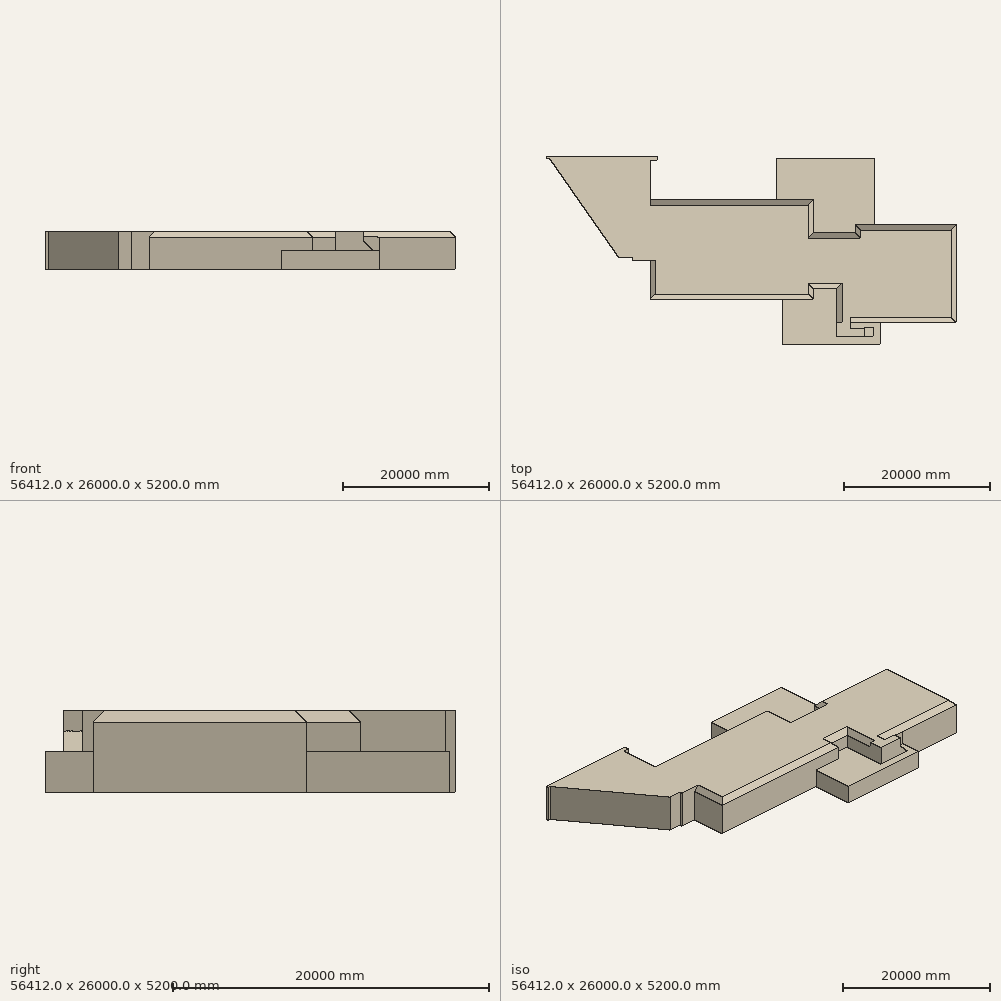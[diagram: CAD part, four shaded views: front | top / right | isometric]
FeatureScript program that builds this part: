
annotation { "Feature Type Name" : "Feature", "Feature Type Description" : "" }
export const myFeature = defineFeature(function(context is Context, id is Id, definition is map)
    precondition{}
    {
        {
            var Q0;
            Q0=qCreatedBy(makeId("Top.planeOp"),FACE);
            var sketch = newSketch(context, id + "F0", { "sketchPlane" : qUnion([Q0])});
            skLineSegment(sketch, "E0", {"start": v(36993.9, 16220.68) * mm, "end": v(36993.9, 2680.68) * mm});
            skLineSegment(sketch, "E1", {"start": v(36993.9, 2680.68) * mm, "end": v(26593.9, 2680.68) * mm});
            skLineSegment(sketch, "E2", {"start": v(26593.9, 2680.68) * mm, "end": v(26593.9, -349.32) * mm});
            skLineSegment(sketch, "E3", {"start": v(26593.9, -349.32) * mm, "end": v(13053.9, -349.32) * mm});
            skLineSegment(sketch, "E4", {"start": v(13053.9, -349.32) * mm, "end": v(13053.9, 5900.68) * mm});
            skLineSegment(sketch, "E5", {"start": v(13053.9, 5900.68) * mm, "end": v(-5146.1, 5900.68) * mm});
            skLineSegment(sketch, "E6", {"start": v(-5146.1, 5900.68) * mm, "end": v(-5146.1, 11220.68) * mm});
            skLineSegment(sketch, "E7", {"start": v(-5146.1, 11220.68) * mm, "end": v(-7546.1, 11220.68) * mm});
            skLineSegment(sketch, "E8", {"start": v(-7546.1, 11220.68) * mm, "end": v(-7546.1, 11620.68) * mm});
            skLineSegment(sketch, "E9", {"start": v(-7546.1, 11620.68) * mm, "end": v(-9442.1, 11620.68) * mm});
            skLineSegment(sketch, "E10", {"start": v(-9442.1, 11620.68) * mm, "end": v(-9442.1, 25270.68) * mm});
            skLineSegment(sketch, "E11", {"start": v(-9442.1, 25270.68) * mm, "end": v(-18978.1, 25270.68) * mm});
            skLineSegment(sketch, "E12", {"start": v(-18978.1, 25270.68) * mm, "end": v(-9442.1, 11620.68) * mm});
            skLineSegment(sketch, "E13", {"start": v(-18978.1, 25270.68) * mm, "end": v(-19418.1, 25270.68) * mm});
            skLineSegment(sketch, "E14", {"start": v(-19418.1, 25270.68) * mm, "end": v(-19418.1, 25650.68) * mm});
            skLineSegment(sketch, "E15", {"start": v(-19418.1, 25650.68) * mm, "end": v(-4148.1, 25650.68) * mm});
            skLineSegment(sketch, "E16", {"start": v(-4148.1, 25650.68) * mm, "end": v(-4148.1, 25040.68) * mm});
            skLineSegment(sketch, "E17", {"start": v(-4148.1, 25040.68) * mm, "end": v(-5048.1, 25040.68) * mm});
            skLineSegment(sketch, "E18", {"start": v(-5048.1, 25040.68) * mm, "end": v(-5048.1, 19620.68) * mm});
            skLineSegment(sketch, "E19", {"start": v(-5048.1, 19620.68) * mm, "end": v(12161.9, 19620.68) * mm});
            skLineSegment(sketch, "E20", {"start": v(12161.9, 19620.68) * mm, "end": v(12161.9, 25270.68) * mm});
            skLineSegment(sketch, "E21", {"start": v(12161.9, 25270.68) * mm, "end": v(25701.9, 25270.68) * mm});
            skLineSegment(sketch, "E22", {"start": v(25701.9, 25270.68) * mm, "end": v(25701.9, 15461.87) * mm});
            skLineSegment(sketch, "E23", {"start": v(36993.9, 16220.68) * mm, "end": v(25701.9, 16220.68) * mm});
            skSolve(sketch);
        }
        {
            var Q0;
            Q0=makeQuery(id+"F0.imprint","IMPRINT",FACE,{"disambiguationData":[TD([[makeQuery(id+"F0.imprint","IMPRINT",EDGE,{"derivedFrom":sQuery(id+"F0.wireOp",EDGE,"E0")}),-1.0]])]});
            var Q1;
            Q1=makeQuery(id+"F0.imprint","IMPRINT",FACE,{"disambiguationData":[TD([[makeQuery(id+"F0.imprint","IMPRINT",EDGE,{"derivedFrom":sQuery(id+"F0.wireOp",EDGE,"E10")}),1.0]])]});
            extrude(context, id + "F1", {"entities" : qUnion([Q0, Q1]), "depth" : 2600 * mm});
        }
        {
            var Q0;
            Q0=makeQuery(id+"F1.opExtrude","CAP_FACE",FACE,{"disambiguationData":[OSD([sQuery(id+"F0.wireOp",EDGE,"E0"),sQuery(id+"F0.wireOp",EDGE,"E1"),sQuery(id+"F0.wireOp",EDGE,"E2"),sQuery(id+"F0.wireOp",EDGE,"E3"),sQuery(id+"F0.wireOp",EDGE,"E4"),sQuery(id+"F0.wireOp",EDGE,"E5"),sQuery(id+"F0.wireOp",EDGE,"E6"),sQuery(id+"F0.wireOp",EDGE,"E7"),sQuery(id+"F0.wireOp",EDGE,"E8"),sQuery(id+"F0.wireOp",EDGE,"E9"),sQuery(id+"F0.wireOp",EDGE,"E12"),sQuery(id+"F0.wireOp",EDGE,"E13"),sQuery(id+"F0.wireOp",EDGE,"E14"),sQuery(id+"F0.wireOp",EDGE,"E15"),sQuery(id+"F0.wireOp",EDGE,"E16"),sQuery(id+"F0.wireOp",EDGE,"E17"),sQuery(id+"F0.wireOp",EDGE,"E18"),sQuery(id+"F0.wireOp",EDGE,"E19"),sQuery(id+"F0.wireOp",EDGE,"E20"),sQuery(id+"F0.wireOp",EDGE,"E21"),sQuery(id+"F0.wireOp",EDGE,"E22"),sQuery(id+"F0.wireOp",EDGE,"E23")])],"isStart":false});
            var sketch = newSketch(context, id + "F2", { "sketchPlane" : qUnion([Q0])});
            skLineSegment(sketch, "E24", {"start": v(12161.9, 19620.68) * mm, "end": v(17361.9, 19620.68) * mm});
            skLineSegment(sketch, "E25", {"start": v(17361.9, 19620.68) * mm, "end": v(17361.9, 15085.94) * mm});
            skLineSegment(sketch, "E26", {"start": v(17361.9, 15085.94) * mm, "end": v(23051.54, 15085.94) * mm});
            skLineSegment(sketch, "E27", {"start": v(23051.54, 15085.94) * mm, "end": v(23051.54, 16220.68) * mm});
            skLineSegment(sketch, "E28", {"start": v(23051.54, 16220.68) * mm, "end": v(25701.9, 16220.68) * mm});
            skLineSegment(sketch, "E29", {"start": v(13053.9, 5900.68) * mm, "end": v(17361.9, 5900.68) * mm});
            skLineSegment(sketch, "E30", {"start": v(17361.9, 5900.68) * mm, "end": v(17361.9, 7372.48) * mm});
            skLineSegment(sketch, "E31", {"start": v(17361.9, 7372.48) * mm, "end": v(20543.7, 7372.48) * mm});
            skLineSegment(sketch, "E32", {"start": v(20543.7, 7372.48) * mm, "end": v(20543.7, 797.7) * mm});
            skLineSegment(sketch, "E33", {"start": v(20543.7, 797.7) * mm, "end": v(24293.76, 797.7) * mm});
            skLineSegment(sketch, "E34", {"start": v(24293.76, 797.7) * mm, "end": v(24293.76, 1966.55) * mm});
            skLineSegment(sketch, "E35", {"start": v(24293.76, 1966.55) * mm, "end": v(22443.08, 1966.55) * mm});
            skLineSegment(sketch, "E36", {"start": v(22443.08, 1966.55) * mm, "end": v(22443.08, 2794.49) * mm});
            skLineSegment(sketch, "E37", {"start": v(22443.08, 2794.49) * mm, "end": v(26593.9, 2680.68) * mm});
            skSolve(sketch);
        }
        {
            var Q0;
            Q0=makeQuery(id+"F2.imprint","IMPRINT",FACE,{"disambiguationData":[TD([[makeQuery(id+"F2.imprint","IMPRINT",EDGE,{"derivedFrom":sQuery(id+"F2.wireOp",EDGE,"E24")}),-1.0]])]});
            extrude(context, id + "F3", {"entities" : qUnion([Q0]), "operationType" : NewBodyOperationType.ADD, "depth" : 2600 * mm});
        }
        {
            var Q0;
            Q0=makeQuery(id+"F3.opExtrude","CAP_FACE",FACE,{"disambiguationData":[OSD([sQuery(id+"F0.wireOp",EDGE,"E0"),sQuery(id+"F0.wireOp",EDGE,"E1"),sQuery(id+"F0.wireOp",EDGE,"E5"),sQuery(id+"F0.wireOp",EDGE,"E6"),sQuery(id+"F0.wireOp",EDGE,"E7"),sQuery(id+"F0.wireOp",EDGE,"E8"),sQuery(id+"F0.wireOp",EDGE,"E9"),sQuery(id+"F0.wireOp",EDGE,"E12"),sQuery(id+"F0.wireOp",EDGE,"E13"),sQuery(id+"F0.wireOp",EDGE,"E14"),sQuery(id+"F0.wireOp",EDGE,"E15"),sQuery(id+"F0.wireOp",EDGE,"E16"),sQuery(id+"F0.wireOp",EDGE,"E17"),sQuery(id+"F0.wireOp",EDGE,"E18"),sQuery(id+"F0.wireOp",EDGE,"E19"),sQuery(id+"F0.wireOp",EDGE,"E23"),sQuery(id+"F2.wireOp",EDGE,"E24"),sQuery(id+"F2.wireOp",EDGE,"E25"),sQuery(id+"F2.wireOp",EDGE,"E26"),sQuery(id+"F2.wireOp",EDGE,"E27"),sQuery(id+"F2.wireOp",EDGE,"E28"),sQuery(id+"F2.wireOp",EDGE,"E29"),sQuery(id+"F2.wireOp",EDGE,"E30"),sQuery(id+"F2.wireOp",EDGE,"E31"),sQuery(id+"F2.wireOp",EDGE,"E32"),sQuery(id+"F2.wireOp",EDGE,"E33"),sQuery(id+"F2.wireOp",EDGE,"E34"),sQuery(id+"F2.wireOp",EDGE,"E35"),sQuery(id+"F2.wireOp",EDGE,"E36"),sQuery(id+"F2.wireOp",EDGE,"E37")])],"isStart":false});
            var sketch = newSketch(context, id + "F4", { "sketchPlane" : qUnion([Q0])});
            skLineSegment(sketch, "E38", {"start": v(22443.08, 2794.49) * mm, "end": v(20543.7, 2794.49) * mm});
            skSolve(sketch);
        }
        {
            var Q0;
            Q0=makeQuery(id+"F3.opExtrude","CAP_EDGE",EDGE,{"disambiguationData":[OSD([sQuery(id+"F0.wireOp",EDGE,"E1")])],"isStart":false});
            var Q1;
            Q1=makeQuery(id+"F3.opExtrude","CAP_EDGE",EDGE,{"disambiguationData":[OSD([sQuery(id+"F2.wireOp",EDGE,"E31")])],"isStart":false});
            var Q2;
            Q2=makeQuery(id+"F3.opExtrude","CAP_EDGE",EDGE,{"disambiguationData":[OSD([sQuery(id+"F2.wireOp",EDGE,"E32")])],"isStart":false});
            var Q3;
            Q3=makeQuery(id+"F3.opExtrude","CAP_EDGE",EDGE,{"disambiguationData":[OSD([sQuery(id+"F2.wireOp",EDGE,"E30")])],"isStart":false});
            var Q4;
            Q4=makeQuery(id+"F3.opExtrude","CAP_EDGE",EDGE,{"disambiguationData":[OSD([sQuery(id+"F0.wireOp",EDGE,"E5"),sQuery(id+"F2.wireOp",EDGE,"E29")])],"isStart":false});
            var Q5;
            Q5=makeQuery(id+"F3.opExtrude","CAP_EDGE",EDGE,{"disambiguationData":[OSD([sQuery(id+"F0.wireOp",EDGE,"E6")])],"isStart":false});
            var Q6;
            Q6=makeQuery(id+"F3.opExtrude","CAP_EDGE",EDGE,{"disambiguationData":[OSD([sQuery(id+"F0.wireOp",EDGE,"E19"),sQuery(id+"F2.wireOp",EDGE,"E24")])],"isStart":false});
            var Q7;
            Q7=makeQuery(id+"F3.opExtrude","CAP_EDGE",EDGE,{"disambiguationData":[OSD([sQuery(id+"F2.wireOp",EDGE,"E25")])],"isStart":false});
            var Q8;
            Q8=makeQuery(id+"F3.opExtrude","CAP_EDGE",EDGE,{"disambiguationData":[OSD([sQuery(id+"F2.wireOp",EDGE,"E26")])],"isStart":false});
            var Q9;
            Q9=makeQuery(id+"F3.opExtrude","CAP_EDGE",EDGE,{"disambiguationData":[OSD([sQuery(id+"F2.wireOp",EDGE,"E27")])],"isStart":false});
            var Q10;
            Q10=makeQuery(id+"F3.opExtrude","CAP_EDGE",EDGE,{"disambiguationData":[OSD([sQuery(id+"F0.wireOp",EDGE,"E23"),sQuery(id+"F2.wireOp",EDGE,"E28")])],"isStart":false});
            var Q11;
            Q11=makeQuery(id+"F3.opExtrude","CAP_EDGE",EDGE,{"disambiguationData":[OSD([sQuery(id+"F0.wireOp",EDGE,"E0")])],"isStart":false});
            chamfer(context, id + "F5", {"entities" : qUnion([Q0, Q1, Q2, Q3, Q4, Q5, Q6, Q7, Q8, Q9, Q10, Q11]), "width" : 750 * mm, "tangentPropagation" : true});
        }
        {
            var Q0;
            Q0=makeQuery(id+"F3.opExtrude","SWEPT_FACE",FACE,{"disambiguationData":[OSD([sQuery(id+"F2.wireOp",EDGE,"E33")])]});
            var sketch = newSketch(context, id + "F6", { "sketchPlane" : qUnion([Q0])});
            skLineSegment(sketch, "E39", {"start": v(22793.73, 5200) * mm, "end": v(22793.73, 2600) * mm});
            skLineSegment(sketch, "E40", {"start": v(24293.76, 3900) * mm, "end": v(25601.25, 2600) * mm});
            skLineSegment(sketch, "E41", {"start": v(25601.25, 2600) * mm, "end": v(24293.76, 2600) * mm});
            skLineSegment(sketch, "E42", {"start": v(24293.76, 2600) * mm, "end": v(24293.76, 3900) * mm});
            skSolve(sketch);
        }
        {
            var Q0;
            Q0 = qSketchRegion(id + "F6", true);
            extrude(context, id + "F7", {"entities" : qUnion([Q0]), "operationType" : NewBodyOperationType.ADD, "oppositeDirection" : true, "depth" : 1200 * mm});
        }
        {
            var Q0;
            {var subQ0=sQuery(id+"F4.wireOp",EDGE,"E38");Q0=makeQuery(id+"F4.imprint","IMPRINT",FACE,{"disambiguationData":[TD([[makeQuery(id+"F4.imprint","IMPRINT",EDGE,{"derivedFrom":subQ0}),1.0]])]});}
            extrude(context, id + "F8", {"entities" : qUnion([Q0]), "operationType" : NewBodyOperationType.ADD, "oppositeDirection" : true, "depth" : 1280 * mm});
        }
    });
